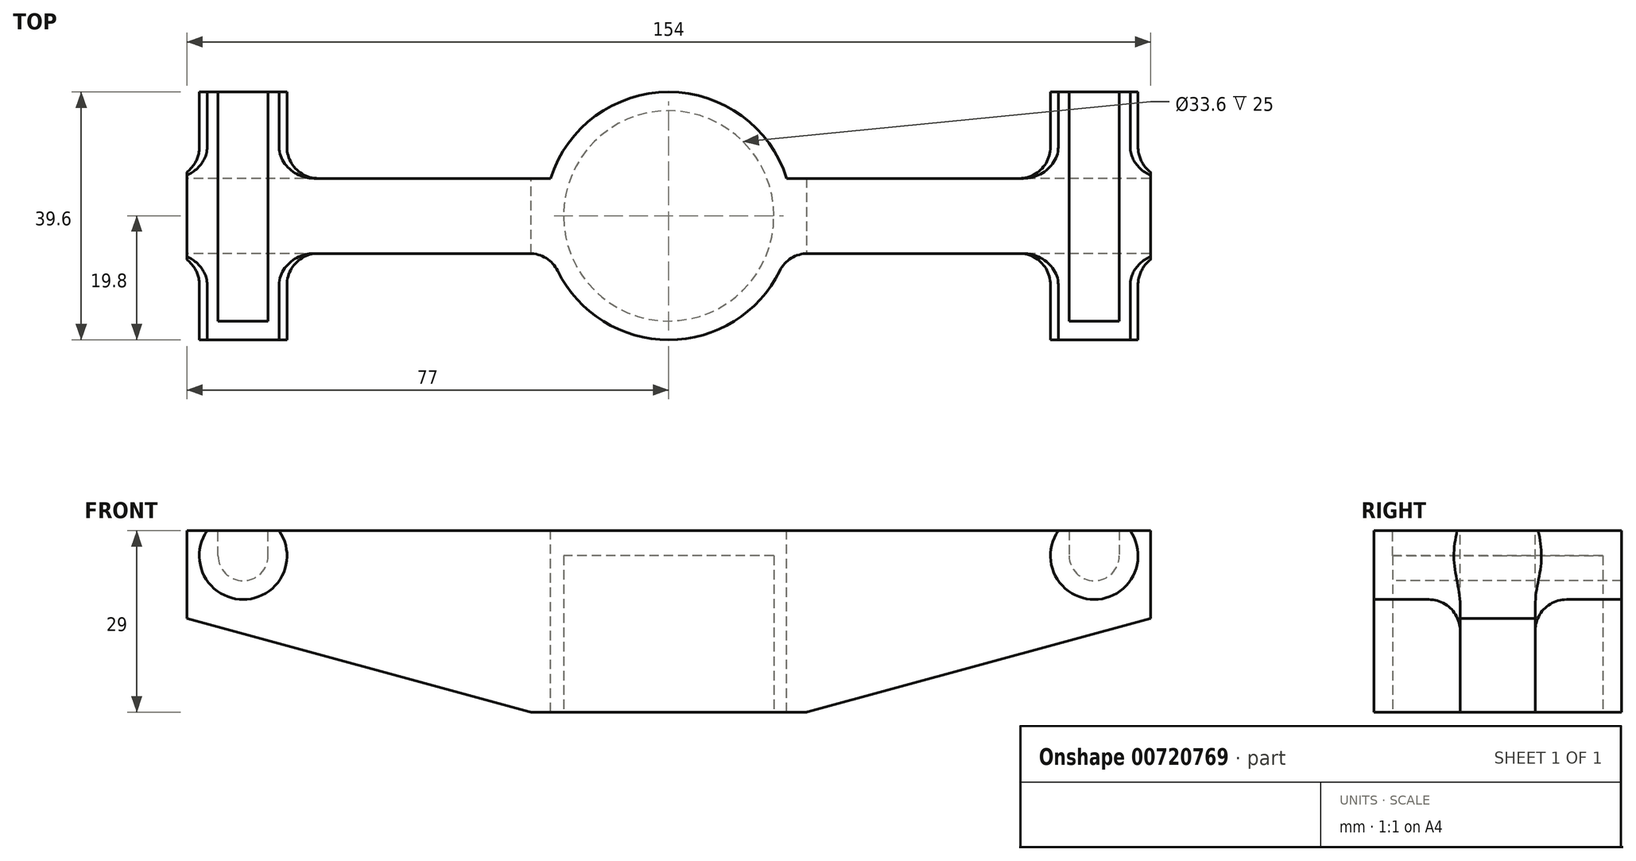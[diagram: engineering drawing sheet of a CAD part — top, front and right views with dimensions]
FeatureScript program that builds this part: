
annotation { "Feature Type Name" : "Feature", "Feature Type Description" : "" }
export const myFeature = defineFeature(function(context is Context, id is Id, definition is map)
    precondition{}
    {
        {
            var Q0;
            Q0=qCreatedBy(makeId("Top.planeOp"),FACE);
            var sketch = newSketch(context, id + "F0", { "sketchPlane" : qUnion([Q0])});
            skCircle(sketch, "E0", {"center": v(0, 0) * mm, "radius": 16.8 * mm});
            skCircle(sketch, "E1", {"center": v(0, 0) * mm, "radius": 19.8 * mm});
            skSolve(sketch);
        }
        {
            var Q0;
            Q0=makeQuery(id+"F0.imprint","IMPRINT",FACE,{"disambiguationData":[TD([[makeQuery(id+"F0.imprint","IMPRINT",EDGE,{"derivedFrom":sQuery(id+"F0.wireOp",EDGE,"E0")}),-1.0]])]});
            extrude(context, id + "F1", {"entities" : qUnion([Q0]), "depth" : 25 * mm, "offsetDistance" : 25 * mm});
        }
        {
            var Q0;
            Q0=makeQuery(id+"F1.opExtrude","CAP_FACE",FACE,{"disambiguationData":[OSD([sQuery(id+"F0.wireOp",EDGE,"E0"),sQuery(id+"F0.wireOp",EDGE,"E1")])],"isStart":false});
            var sketch = newSketch(context, id + "F2", { "sketchPlane" : qUnion([Q0])});
            skSolve(sketch);
        }
        {
            var Q0;
            Q0=makeQuery(id+"F2.imprint","IMPRINT",FACE,{"disambiguationData":[TD([[makeQuery(id+"F2.imprint","IMPRINT",EDGE,{"derivedFrom":makeQuery(id+"F1.opExtrude","CAP_EDGE",EDGE,{"disambiguationData":[OSD([sQuery(id+"F0.wireOp",EDGE,"E0")])],"isStart":false})}),-1.0]])]});
            var Q1;
            Q1=makeQuery(id+"F2.imprint","IMPRINT",FACE,{"disambiguationData":[TD([[makeQuery(id+"F2.imprint","IMPRINT",EDGE,{"derivedFrom":makeQuery(id+"F1.opExtrude","CAP_EDGE",EDGE,{"disambiguationData":[OSD([sQuery(id+"F0.wireOp",EDGE,"E0")])],"isStart":false})}),1.0]])]});
            extrude(context, id + "F3", {"entities" : qUnion([Q0, Q1]), "operationType" : NewBodyOperationType.ADD, "depth" : 4 * mm, "offsetDistance" : 25 * mm});
        }
        {
            var Q0;
            Q0=makeQuery(id+"F3.opExtrude","CAP_FACE",FACE,{"disambiguationData":[OSD([sQuery(id+"F0.wireOp",EDGE,"E1")])],"isStart":false});
            var sketch = newSketch(context, id + "F4", { "sketchPlane" : qUnion([Q0])});
            skPoint(sketch, "E2", {"position": v(0, 0) * mm});
            skLineSegment(sketch, "E3.bottom", {"start": v(77, -6) * mm, "end": v(-77, -6) * mm});
            skLineSegment(sketch, "E3.top", {"start": v(77, 6) * mm, "end": v(-77, 6) * mm});
            skLineSegment(sketch, "E3.left", {"start": v(77, -6) * mm, "end": v(77, 6) * mm});
            skLineSegment(sketch, "E3.right", {"start": v(-77, -6) * mm, "end": v(-77, 6) * mm});
            skSolve(sketch);
        }
        {
            var Q0;
            {var subQ0=sQuery(id+"F4.wireOp",EDGE,"E3.right");Q0=makeQuery(id+"F4.imprint","IMPRINT",FACE,{"disambiguationData":[TD([[makeQuery(id+"F4.imprint","IMPRINT",EDGE,{"derivedFrom":subQ0}),-1.0]])]});}
            var Q1;
            {var subQ0=sQuery(id+"F4.wireOp",EDGE,"E3.left");Q1=makeQuery(id+"F4.imprint","IMPRINT",FACE,{"disambiguationData":[TD([[makeQuery(id+"F4.imprint","IMPRINT",EDGE,{"derivedFrom":subQ0}),1.0]])]});}
            extrude(context, id + "F5", {"entities" : qUnion([Q0, Q1]), "operationType" : NewBodyOperationType.ADD, "oppositeDirection" : true, "depth" : 29 * mm, "offsetDistance" : 25 * mm});
        }
        {
            var Q0;
            Q0=makeQuery(id+"F5.opExtrude","CAP_EDGE",EDGE,{"disambiguationData":[OSD([sQuery(id+"F4.wireOp",EDGE,"E3.left")])],"isStart":false});
            var Q1;
            Q1=makeQuery(id+"F5.opExtrude","CAP_EDGE",EDGE,{"disambiguationData":[OSD([sQuery(id+"F4.wireOp",EDGE,"E3.right")])],"isStart":false});
            chamfer(context, id + "F6", {"entities" : qUnion([Q0, Q1]), "chamferType" : ChamferType.TWO_OFFSETS, "width1" : 15 * mm, "oppositeDirection" : false, "width2" : 55 * mm, "tangentPropagation" : true});
        }
        {
            var Q0;
            {var subQ0=sQuery(id+"F4.wireOp",EDGE,"E3.top");var subQ1=sQuery(id+"F0.wireOp",EDGE,"E1");Q0=makeQuery(id+"F5.opExtrude","SWEPT_EDGE",EDGE,{"disambiguationData":[OSD([subQ1,subQ0]),TDD([makeQuery(id+"F4.imprint","INTERSECT",VERTEX,{"disambiguationData":[OD(1.0)],"derivedFrom":[makeQuery(id+"F3.opExtrude","CAP_EDGE",EDGE,{"disambiguationData":[OSD([subQ1])],"isStart":false}),subQ0]})])]});}
            var Q1;
            {var subQ0=sQuery(id+"F4.wireOp",EDGE,"E3.top");var subQ1=sQuery(id+"F0.wireOp",EDGE,"E1");Q1=makeQuery(id+"F5.opExtrude","SWEPT_EDGE",EDGE,{"disambiguationData":[OSD([subQ1,subQ0]),TDD([makeQuery(id+"F4.imprint","INTERSECT",VERTEX,{"disambiguationData":[OD(0.0)],"derivedFrom":[makeQuery(id+"F3.opExtrude","CAP_EDGE",EDGE,{"disambiguationData":[OSD([subQ1])],"isStart":false}),subQ0]})])]});}
            var Q2;
            {var subQ0=sQuery(id+"F4.wireOp",EDGE,"E3.bottom");var subQ1=sQuery(id+"F0.wireOp",EDGE,"E1");Q2=makeQuery(id+"F5.opExtrude","SWEPT_EDGE",EDGE,{"disambiguationData":[OSD([subQ1,subQ0]),TDD([makeQuery(id+"F4.imprint","INTERSECT",VERTEX,{"disambiguationData":[OD(0.0)],"derivedFrom":[makeQuery(id+"F3.opExtrude","CAP_EDGE",EDGE,{"disambiguationData":[OSD([subQ1])],"isStart":false}),subQ0]})])]});}
            var Q3;
            {var subQ0=sQuery(id+"F4.wireOp",EDGE,"E3.bottom");var subQ1=sQuery(id+"F0.wireOp",EDGE,"E1");Q3=makeQuery(id+"F5.opExtrude","SWEPT_EDGE",EDGE,{"disambiguationData":[OSD([subQ1,subQ0]),TDD([makeQuery(id+"F4.imprint","INTERSECT",VERTEX,{"disambiguationData":[OD(1.0)],"derivedFrom":[makeQuery(id+"F3.opExtrude","CAP_EDGE",EDGE,{"disambiguationData":[OSD([subQ1])],"isStart":false}),subQ0]})])]});}
            fillet(context, id + "F7", {"entities" : qUnion([Q0, Q1, Q2, Q3]), "radius" : 5 * mm, "tangentPropagation" : true, "allowEdgeOverflow" : false});
        }
        {
            var Q0;
            {var subQ0=sQuery(id+"F4.wireOp",EDGE,"E3.bottom");Q0=makeQuery(id+"F5.opExtrude","SWEPT_FACE",FACE,{"disambiguationData":[OSD([subQ0]),TDD([makeQuery(id+"F4.imprint","IMPRINT",EDGE,{"disambiguationData":[TD([[makeQuery(id+"F4.imprint","INTERSECT",VERTEX,{"derivedFrom":[subQ0,sQuery(id+"F4.wireOp",EDGE,"E3.right")]}),1.0]])],"derivedFrom":subQ0})])]});}
            var sketch = newSketch(context, id + "F8", { "sketchPlane" : qUnion([Q0])});
            skCircle(sketch, "E4", {"center": v(-68, 25) * mm, "radius": 4 * mm});
            skCircle(sketch, "E5", {"center": v(68, 25) * mm, "radius": 4 * mm});
            skLineSegment(sketch, "E6", {"start": v(-72, 25) * mm, "end": v(-72, 29) * mm});
            skLineSegment(sketch, "E7", {"start": v(-64, 25) * mm, "end": v(-64, 29) * mm});
            skLineSegment(sketch, "E8", {"start": v(72, 29) * mm, "end": v(72, 25) * mm});
            skLineSegment(sketch, "E9", {"start": v(64, 29) * mm, "end": v(64, 25) * mm});
            skLineSegment(sketch, "E10", {"start": v(64, 29) * mm, "end": v(72, 29) * mm});
            skCircle(sketch, "E11", {"center": v(-68, 25) * mm, "radius": 7 * mm});
            skCircle(sketch, "E12", {"center": v(68, 25) * mm, "radius": 7 * mm});
            skLineSegment(sketch, "E13", {"start": v(-73.74, 29) * mm, "end": v(-62.26, 29) * mm});
            skLineSegment(sketch, "E14", {"start": v(62.26, 29) * mm, "end": v(73.74, 29) * mm});
            skSolve(sketch);
        }
        {
            var Q0;
            {var subQ0=sQuery(id+"F8.wireOp",EDGE,"E8");Q0=makeQuery(id+"F8.imprint","IMPRINT",FACE,{"disambiguationData":[TD([[makeQuery(id+"F8.imprint","IMPRINT",EDGE,{"derivedFrom":subQ0}),-1.0]])]});}
            var Q1;
            {var subQ0=sQuery(id+"F8.wireOp",EDGE,"E9");Q1=makeQuery(id+"F8.imprint","IMPRINT",FACE,{"disambiguationData":[TD([[makeQuery(id+"F8.imprint","IMPRINT",EDGE,{"derivedFrom":subQ0}),1.0]])]});}
            var Q2;
            {var subQ0=sQuery(id+"F8.wireOp",EDGE,"E5");var subQ1=makeQuery(id+"F8.imprint","INTERSECT",VERTEX,{"derivedFrom":[subQ0,sQuery(id+"F8.wireOp",EDGE,"E8")]});Q2=makeQuery(id+"F8.imprint","IMPRINT",FACE,{"disambiguationData":[TD([[makeQuery(id+"F8.imprint","IMPRINT",EDGE,{"disambiguationData":[TD([[subQ1,-1.0]])],"derivedFrom":subQ0}),1.0]])]});}
            var Q3;
            {var subQ0=sQuery(id+"F8.wireOp",EDGE,"E6");Q3=makeQuery(id+"F8.imprint","IMPRINT",FACE,{"disambiguationData":[TD([[makeQuery(id+"F8.imprint","IMPRINT",EDGE,{"derivedFrom":subQ0}),-1.0]])]});}
            var Q4;
            {var subQ0=sQuery(id+"F8.wireOp",EDGE,"E7");Q4=makeQuery(id+"F8.imprint","IMPRINT",FACE,{"disambiguationData":[TD([[makeQuery(id+"F8.imprint","IMPRINT",EDGE,{"derivedFrom":subQ0}),1.0]])]});}
            var Q5;
            {var subQ0=sQuery(id+"F8.wireOp",EDGE,"E4");var subQ4=makeQuery(id+"F8.imprint","INTERSECT",VERTEX,{"derivedFrom":[subQ0,sQuery(id+"F8.wireOp",EDGE,"E6")]});Q5=makeQuery(id+"F8.imprint","IMPRINT",FACE,{"disambiguationData":[TD([[makeQuery(id+"F8.imprint","IMPRINT",EDGE,{"disambiguationData":[TD([[subQ4,-1.0]])],"derivedFrom":subQ0}),1.0]])]});}
            extrude(context, id + "F9", {"entities" : qUnion([Q0, Q1, Q2, Q3, Q4, Q5]), "operationType" : NewBodyOperationType.REMOVE, "oppositeDirection" : true, "depth" : 25 * mm, "offsetDistance" : 25 * mm});
        }
        {
            var Q0;
            {var subQ7=sQuery(id+"F8.wireOp",EDGE,"E6");Q0=makeQuery(id+"F8.imprint","IMPRINT",FACE,{"disambiguationData":[TD([[makeQuery(id+"F8.imprint","IMPRINT",EDGE,{"derivedFrom":subQ7}),1.0]])]});}
            var Q1;
            {var subQ5=sQuery(id+"F8.wireOp",EDGE,"E8");Q1=makeQuery(id+"F8.imprint","IMPRINT",FACE,{"disambiguationData":[TD([[makeQuery(id+"F8.imprint","IMPRINT",EDGE,{"derivedFrom":subQ5}),1.0]])]});}
            extrude(context, id + "F10", {"entities" : qUnion([Q0, Q1]), "operationType" : NewBodyOperationType.ADD, "depth" : 13.8 * mm, "offsetDistance" : 25 * mm, "hasSecondDirection" : true, "secondDirectionOppositeDirection" : true, "secondDirectionDepth" : 25.8 * mm});
        }
        {
            var Q0;
            {var subQ0=sQuery(id+"F4.wireOp",EDGE,"E3.top");Q0=makeQuery(id+"F10.boolean.opBoolean","INTERSECT",EDGE,{"derivedFrom":[makeQuery(id+"F5.opExtrude","SWEPT_FACE",FACE,{"disambiguationData":[OSD([subQ0]),TDD([makeQuery(id+"F4.imprint","IMPRINT",EDGE,{"disambiguationData":[TD([[makeQuery(id+"F4.imprint","INTERSECT",VERTEX,{"derivedFrom":[subQ0,sQuery(id+"F4.wireOp",EDGE,"E3.left")]}),-1.0]])],"derivedFrom":subQ0})])]}),makeQuery(id+"F10.opExtrude","SWEPT_FACE",FACE,{"disambiguationData":[OSD([sQuery(id+"F8.wireOp",EDGE,"E12")])]})]});}
            var Q1;
            {var subQ0=sQuery(id+"F4.wireOp",EDGE,"E3.bottom");Q1=makeQuery(id+"F10.boolean.opBoolean","INTERSECT",EDGE,{"derivedFrom":[makeQuery(id+"F5.opExtrude","SWEPT_FACE",FACE,{"disambiguationData":[OSD([subQ0]),TDD([makeQuery(id+"F4.imprint","IMPRINT",EDGE,{"disambiguationData":[TD([[makeQuery(id+"F4.imprint","INTERSECT",VERTEX,{"derivedFrom":[subQ0,sQuery(id+"F4.wireOp",EDGE,"E3.left")]}),-1.0]])],"derivedFrom":subQ0})])]}),makeQuery(id+"F10.opExtrude","SWEPT_FACE",FACE,{"disambiguationData":[OSD([sQuery(id+"F8.wireOp",EDGE,"E12")])]})]});}
            var Q2;
            {var subQ0=sQuery(id+"F4.wireOp",EDGE,"E3.top");Q2=makeQuery(id+"F10.boolean.opBoolean","INTERSECT",EDGE,{"derivedFrom":[makeQuery(id+"F5.opExtrude","SWEPT_FACE",FACE,{"disambiguationData":[OSD([subQ0]),TDD([makeQuery(id+"F4.imprint","IMPRINT",EDGE,{"disambiguationData":[TD([[makeQuery(id+"F4.imprint","INTERSECT",VERTEX,{"derivedFrom":[subQ0,sQuery(id+"F4.wireOp",EDGE,"E3.right")]}),1.0]])],"derivedFrom":subQ0})])]}),makeQuery(id+"F10.opExtrude","SWEPT_FACE",FACE,{"disambiguationData":[OSD([sQuery(id+"F8.wireOp",EDGE,"E11")])]})]});}
            var Q3;
            {var subQ0=sQuery(id+"F4.wireOp",EDGE,"E3.bottom");Q3=makeQuery(id+"F10.boolean.opBoolean","INTERSECT",EDGE,{"derivedFrom":[makeQuery(id+"F5.opExtrude","SWEPT_FACE",FACE,{"disambiguationData":[OSD([subQ0]),TDD([makeQuery(id+"F4.imprint","IMPRINT",EDGE,{"disambiguationData":[TD([[makeQuery(id+"F4.imprint","INTERSECT",VERTEX,{"derivedFrom":[subQ0,sQuery(id+"F4.wireOp",EDGE,"E3.right")]}),1.0]])],"derivedFrom":subQ0})])]}),makeQuery(id+"F10.opExtrude","SWEPT_FACE",FACE,{"disambiguationData":[OSD([sQuery(id+"F8.wireOp",EDGE,"E11")])]})]});}
            fillet(context, id + "F11", {"entities" : qUnion([Q0, Q1, Q2, Q3]), "radius" : 5 * mm, "tangentPropagation" : true, "allowEdgeOverflow" : false});
        }
        {
            var Q0;
            Q0=makeQuery(id+"F10.opExtrude","CAP_FACE",FACE,{"disambiguationData":[OSD([sQuery(id+"F8.wireOp",EDGE,"E4"),sQuery(id+"F8.wireOp",EDGE,"E6"),sQuery(id+"F8.wireOp",EDGE,"E7"),sQuery(id+"F8.wireOp",EDGE,"E11"),sQuery(id+"F8.wireOp",EDGE,"E13")])],"isStart":false});
            var sketch = newSketch(context, id + "F12", { "sketchPlane" : qUnion([Q0])});
            skLineSegment(sketch, "E15.bottom", {"start": v(-72, 29) * mm, "end": v(-64, 29) * mm});
            skLineSegment(sketch, "E15.top", {"start": v(-72, 21) * mm, "end": v(-64, 21) * mm});
            skLineSegment(sketch, "E15.left", {"start": v(-72, 29) * mm, "end": v(-72, 21) * mm});
            skLineSegment(sketch, "E15.right", {"start": v(-64, 29) * mm, "end": v(-64, 21) * mm});
            skLineSegment(sketch, "E16.bottom", {"start": v(64, 29) * mm, "end": v(72, 29) * mm});
            skLineSegment(sketch, "E16.top", {"start": v(64, 21) * mm, "end": v(72, 21) * mm});
            skLineSegment(sketch, "E16.left", {"start": v(64, 29) * mm, "end": v(64, 21) * mm});
            skLineSegment(sketch, "E16.right", {"start": v(72, 29) * mm, "end": v(72, 21) * mm});
            skSolve(sketch);
        }
        {
            var Q0;
            Q0=makeQuery(id+"F12.imprint","IMPRINT",FACE,{"disambiguationData":[TD([[makeQuery(id+"F12.imprint","IMPRINT",EDGE,{"derivedFrom":sQuery(id+"F12.wireOp",EDGE,"E16.bottom")}),-1.0]])]});
            var Q1;
            {var subQ4=sQuery(id+"F12.wireOp",EDGE,"E15.bottom");Q1=makeQuery(id+"F12.imprint","IMPRINT",FACE,{"disambiguationData":[TD([[makeQuery(id+"F12.imprint","IMPRINT",EDGE,{"derivedFrom":subQ4}),-1.0]])]});}
            var Q2;
            {var subQ0=sQuery(id+"F12.wireOp",EDGE,"E15.right");var subQ1=sQuery(id+"F12.wireOp",EDGE,"E15.top");var subQ2=makeQuery(id+"F12.imprint","INTERSECT",VERTEX,{"derivedFrom":[subQ1,subQ0]});Q2=makeQuery(id+"F12.imprint","IMPRINT",FACE,{"disambiguationData":[TD([[makeQuery(id+"F12.imprint","IMPRINT",EDGE,{"disambiguationData":[TD([[subQ2,1.0]])],"derivedFrom":subQ1}),1.0]])]});}
            var Q3;
            {var subQ0=sQuery(id+"F12.wireOp",EDGE,"E15.left");var subQ1=sQuery(id+"F12.wireOp",EDGE,"E15.top");var subQ2=makeQuery(id+"F12.imprint","INTERSECT",VERTEX,{"derivedFrom":[subQ1,subQ0]});Q3=makeQuery(id+"F12.imprint","IMPRINT",FACE,{"disambiguationData":[TD([[makeQuery(id+"F12.imprint","IMPRINT",EDGE,{"disambiguationData":[TD([[subQ2,-1.0]])],"derivedFrom":subQ1}),1.0]])]});}
            extrude(context, id + "F13", {"entities" : qUnion([Q0, Q1, Q2, Q3]), "operationType" : NewBodyOperationType.ADD, "oppositeDirection" : true, "depth" : 3 * mm, "offsetDistance" : 25 * mm});
        }
    });
